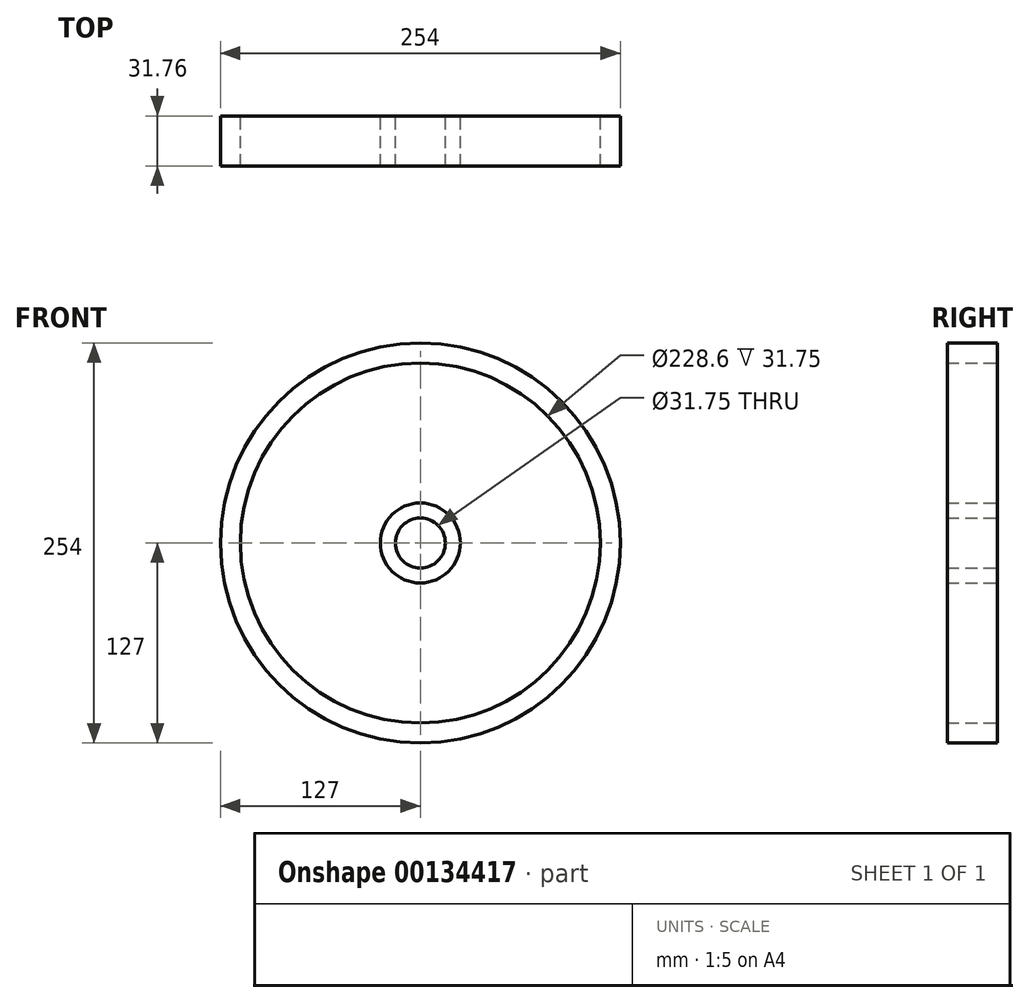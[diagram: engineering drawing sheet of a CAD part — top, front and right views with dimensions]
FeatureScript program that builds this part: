
annotation { "Feature Type Name" : "Feature", "Feature Type Description" : "" }
export const myFeature = defineFeature(function(context is Context, id is Id, definition is map)
    precondition{}
    {
        {
            var Q0;
            Q0=qCreatedBy(makeId("Front.planeOp"),FACE);
            var sketch = newSketch(context, id + "F0", { "sketchPlane" : qUnion([Q0])});
            skCircle(sketch, "E0", {"center": v(0, 0) * mm, "radius": 127 * mm});
            skCircle(sketch, "E1", {"center": v(0, 0) * mm, "radius": 114.3 * mm});
            skCircle(sketch, "E2", {"center": v(0, 0) * mm, "radius": 25.4 * mm});
            skLineSegment(sketch, "E3", {"start": v(-4.94, 24.91) * mm, "end": v(-4.94, 114.2) * mm});
            skLineSegment(sketch, "E4", {"start": v(4.94, 24.91) * mm, "end": v(4.94, 114.2) * mm});
            skLineSegment(sketch, "E5", {"start": v(-25.4, 0) * mm, "end": v(-105.95, -42.9) * mm});
            skLineSegment(sketch, "E6", {"start": v(-20.7, -14.7) * mm, "end": v(-99.32, -56.57) * mm});
            skLineSegment(sketch, "E7", {"start": v(18.92, -18.7) * mm, "end": v(99.6, -56.06) * mm});
            skLineSegment(sketch, "E8", {"start": v(23.27, -10.18) * mm, "end": v(105.95, -42.88) * mm});
            skCircle(sketch, "E9", {"center": v(0, 0) * mm, "radius": 15.88 * mm});
            skSolve(sketch);
        }
        {
            var Q0;
            Q0 = qSketchRegion(id + "F0", true);
            var Q1;
            Q1=makeQuery(id+"F0.imprint","IMPRINT",FACE,{"disambiguationData":[TD([[makeQuery(id+"F0.imprint","IMPRINT",EDGE,{"derivedFrom":sQuery(id+"F0.wireOp",EDGE,"E9")}),-1.0]])]});
            extrude(context, id + "F1", {"entities" : qUnion([Q0, Q1]), "endBound" : BoundingType.SYMMETRIC, "depth" : 31.75 * mm});
        }
    });
